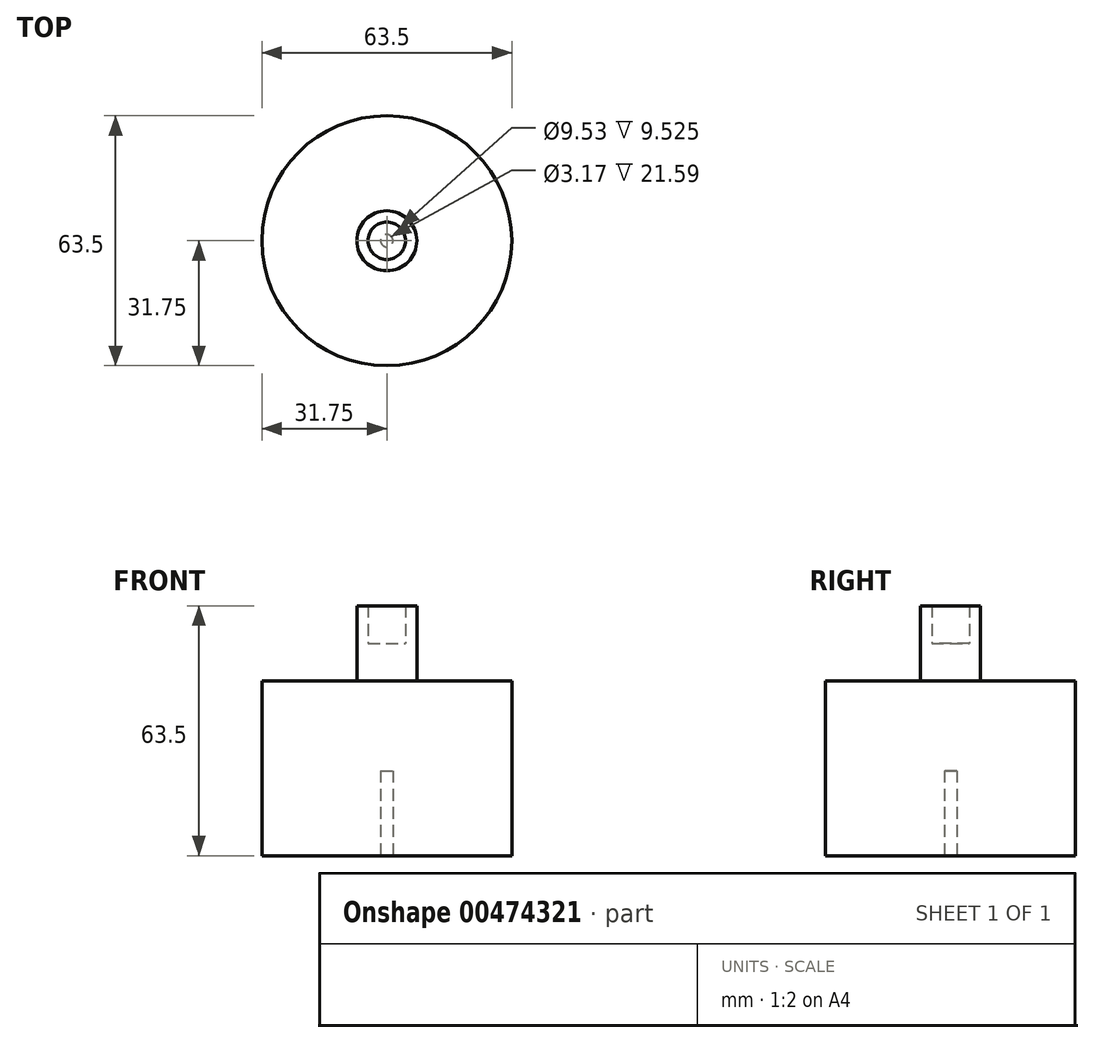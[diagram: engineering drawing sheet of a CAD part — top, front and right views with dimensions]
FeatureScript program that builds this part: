
annotation { "Feature Type Name" : "Feature", "Feature Type Description" : "" }
export const myFeature = defineFeature(function(context is Context, id is Id, definition is map)
    precondition{}
    {
        {
            var Q0;
            Q0=qCreatedBy(makeId("Front.planeOp"),FACE);
            var sketch = newSketch(context, id + "F0", { "sketchPlane" : qUnion([Q0])});
            skLineSegment(sketch, "E0", {"start": v(0, 0) * mm, "end": v(0, 63.5) * mm});
            skLineSegment(sketch, "E1", {"start": v(0, 0) * mm, "end": v(31.75, 0) * mm});
            skLineSegment(sketch, "E2", {"start": v(31.75, 0) * mm, "end": v(31.75, 44.45) * mm});
            skLineSegment(sketch, "E3", {"start": v(0, 63.5) * mm, "end": v(7.62, 63.5) * mm});
            skLineSegment(sketch, "E4", {"start": v(31.75, 44.45) * mm, "end": v(7.62, 44.45) * mm});
            skLineSegment(sketch, "E5", {"start": v(7.62, 44.45) * mm, "end": v(7.62, 63.5) * mm});
            skLineSegment(sketch, "E6", {"start": v(0, 63.5) * mm, "end": v(4.76, 63.5) * mm});
            skLineSegment(sketch, "E7", {"start": v(4.76, 63.5) * mm, "end": v(4.76, 53.98) * mm});
            skLineSegment(sketch, "E8", {"start": v(4.76, 53.98) * mm, "end": v(0, 53.98) * mm});
            skLineSegment(sketch, "E9", {"start": v(0, 0) * mm, "end": v(0, 21.59) * mm});
            skLineSegment(sketch, "E10", {"start": v(0, 21.59) * mm, "end": v(1.59, 21.59) * mm});
            skLineSegment(sketch, "E11", {"start": v(1.59, 21.59) * mm, "end": v(1.59, 0) * mm});
            skSolve(sketch);
        }
        {
            var Q0;
            {var subQ0=sQuery(id+"F0.wireOp",EDGE,"E2");Q0=makeQuery(id+"F0.imprint","IMPRINT",FACE,{"disambiguationData":[TD([[makeQuery(id+"F0.imprint","IMPRINT",EDGE,{"derivedFrom":subQ0}),1.0]])]});}
            var Q1;
            Q1=sQuery(id+"F0.wireOp",EDGE,"E0");
            revolve(context, id + "F1", {"entities" : qUnion([Q0]), "axis" : qUnion([Q1]), "revolveType" : RevolveType.FULL});
        }
    });
